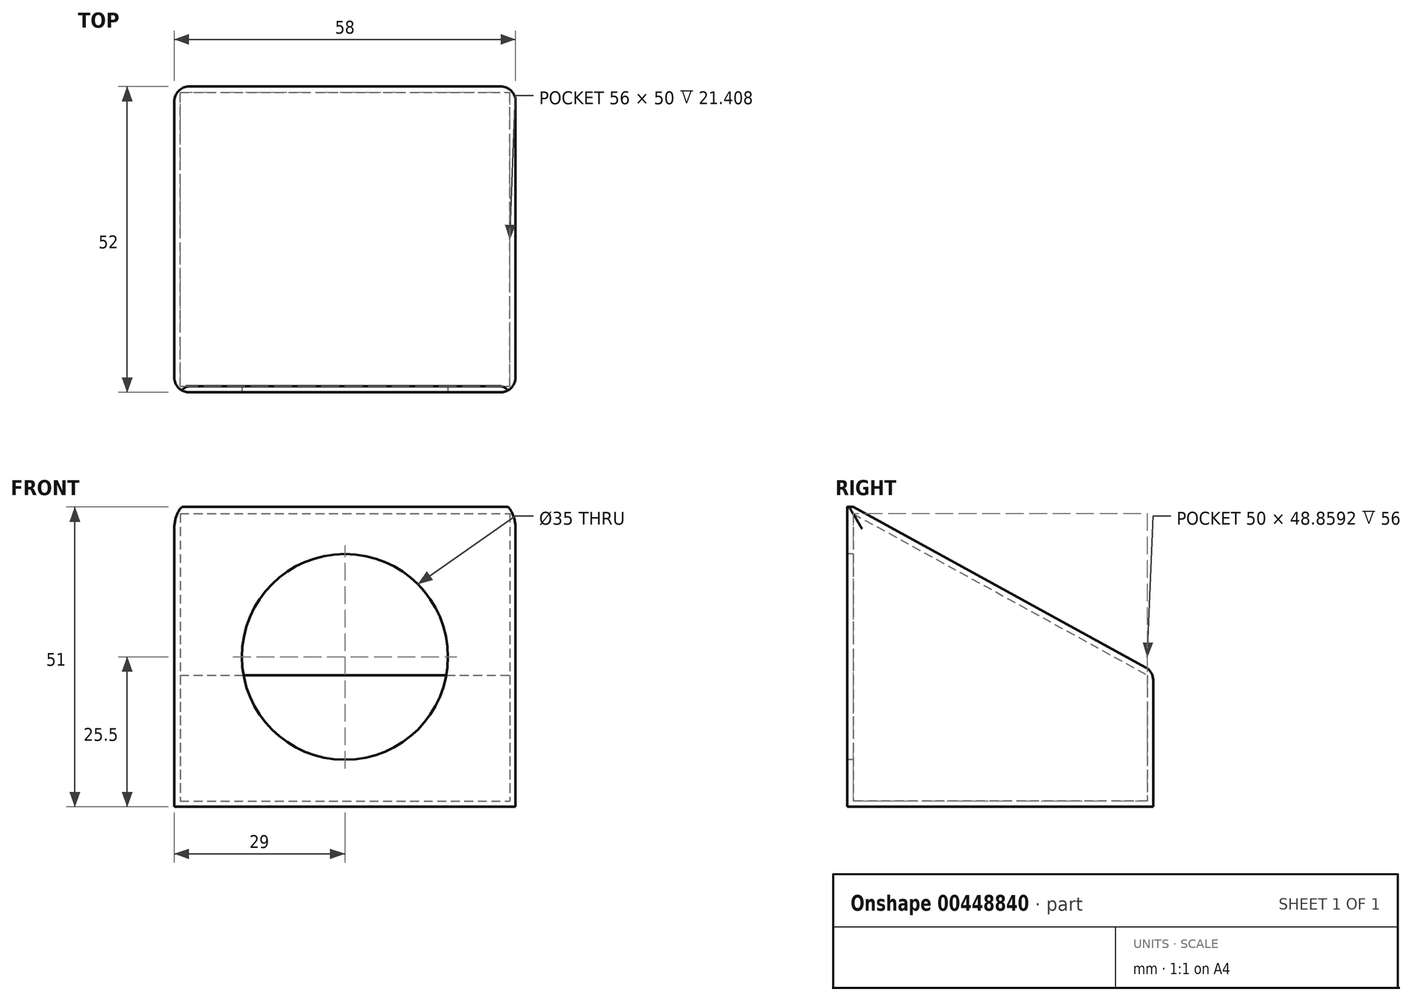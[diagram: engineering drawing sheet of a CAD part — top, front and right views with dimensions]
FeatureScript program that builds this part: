
annotation { "Feature Type Name" : "Feature", "Feature Type Description" : "" }
export const myFeature = defineFeature(function(context is Context, id is Id, definition is map)
    precondition{}
    {
        {
            var Q0;
            Q0=qCreatedBy(makeId("Top.planeOp"),FACE);
            var sketch = newSketch(context, id + "F0", { "sketchPlane" : qUnion([Q0])});
            skLineSegment(sketch, "E0.bottom", {"start": v(29, 26) * mm, "end": v(-29, 26) * mm});
            skLineSegment(sketch, "E0.top", {"start": v(29, -26) * mm, "end": v(-29, -26) * mm});
            skLineSegment(sketch, "E0.left", {"start": v(29, 26) * mm, "end": v(29, -26) * mm});
            skLineSegment(sketch, "E0.right", {"start": v(-29, 26) * mm, "end": v(-29, -26) * mm});
            skPoint(sketch, "E0.middle", {"position": v(0, 0) * mm});
            skSolve(sketch);
        }
        {
            var Q0;
            Q0=makeQuery(id+"F0.imprint","IMPRINT",FACE,{"disambiguationData":[TD([[makeQuery(id+"F0.imprint","IMPRINT",EDGE,{"derivedFrom":sQuery(id+"F0.wireOp",EDGE,"E0.bottom")}),1.0]])]});
            extrude(context, id + "F1", {"entities" : qUnion([Q0]), "depth" : 1 * mm});
        }
        {
            var Q0;
            Q0=makeQuery(id+"F1.opExtrude","CAP_FACE",FACE,{"disambiguationData":[OSD([sQuery(id+"F0.wireOp",EDGE,"E0.bottom"),sQuery(id+"F0.wireOp",EDGE,"E0.top"),sQuery(id+"F0.wireOp",EDGE,"E0.left"),sQuery(id+"F0.wireOp",EDGE,"E0.right")])],"isStart":false});
            var sketch = newSketch(context, id + "F2", { "sketchPlane" : qUnion([Q0])});
            skLineSegment(sketch, "E1", {"start": v(-29, 26) * mm, "end": v(-29, 25) * mm});
            skLineSegment(sketch, "E2", {"start": v(-29, 25) * mm, "end": v(29, 25) * mm});
            skLineSegment(sketch, "E3", {"start": v(-29, -26) * mm, "end": v(-29, -25) * mm});
            skLineSegment(sketch, "E4", {"start": v(-29, -25) * mm, "end": v(29, -25) * mm});
            skLineSegment(sketch, "E5", {"start": v(29, -25) * mm, "end": v(28, -25) * mm});
            skLineSegment(sketch, "E6", {"start": v(28, -25) * mm, "end": v(28, 25) * mm});
            skLineSegment(sketch, "E7", {"start": v(-29, -25) * mm, "end": v(-28, -25) * mm});
            skLineSegment(sketch, "E8", {"start": v(-28, -25) * mm, "end": v(-28, 25) * mm});
            skSolve(sketch);
        }
        {
            var Q0;
            Q0=makeQuery(id+"F2.imprint","IMPRINT",FACE,{"disambiguationData":[TD([[makeQuery(id+"F2.imprint","IMPRINT",EDGE,{"derivedFrom":sQuery(id+"F2.wireOp",EDGE,"E1")}),1.0]])]});
            extrude(context, id + "F3", {"entities" : qUnion([Q0]), "operationType" : NewBodyOperationType.ADD, "depth" : 22 * mm});
        }
        {
            var Q0;
            Q0=makeQuery(id+"F2.imprint","IMPRINT",FACE,{"disambiguationData":[TD([[makeQuery(id+"F2.imprint","IMPRINT",EDGE,{"derivedFrom":sQuery(id+"F2.wireOp",EDGE,"E3")}),1.0]])]});
            extrude(context, id + "F4", {"entities" : qUnion([Q0]), "operationType" : NewBodyOperationType.ADD, "depth" : 50 * mm});
        }
        {
            var Q0;
            Q0=makeQuery(id+"F4.boolean.opBoolean","MERGE",FACE,{"derivedFrom":[makeQuery(id+"F3.boolean.opBoolean","MERGE",FACE,{"derivedFrom":[makeQuery(id+"F1.opExtrude","SWEPT_FACE",FACE,{"disambiguationData":[OSD([sQuery(id+"F0.wireOp",EDGE,"E0.right")])]}),makeQuery(id+"F3.opExtrude","SWEPT_FACE",FACE,{"disambiguationData":[OSD([sQuery(id+"F2.wireOp",EDGE,"E1")])]})]}),makeQuery(id+"F4.opExtrude","SWEPT_FACE",FACE,{"disambiguationData":[OSD([sQuery(id+"F2.wireOp",EDGE,"E3")])]})]});
            var sketch = newSketch(context, id + "F5", { "sketchPlane" : qUnion([Q0])});
            skLineSegment(sketch, "E9", {"start": v(-26, 23) * mm, "end": v(25, 51) * mm});
            skSolve(sketch);
        }
        {
            var Q0;
            Q0=makeQuery(id+"F5.imprint","IMPRINT",FACE,{"disambiguationData":[TD([[makeQuery(id+"F5.imprint","IMPRINT",EDGE,{"derivedFrom":sQuery(id+"F5.wireOp",EDGE,"E9")}),-1.0]])]});
            extrude(context, id + "F6", {"entities" : qUnion([Q0]), "operationType" : NewBodyOperationType.ADD, "oppositeDirection" : true, "depth" : 1 * mm});
        }
        {
            var Q0;
            {var subQ0=sQuery(id+"F0.wireOp",EDGE,"E0.left");Q0=makeQuery(id+"F4.boolean.opBoolean","MERGE",FACE,{"derivedFrom":[makeQuery(id+"F3.boolean.opBoolean","MERGE",FACE,{"derivedFrom":[makeQuery(id+"F1.opExtrude","SWEPT_FACE",FACE,{"disambiguationData":[OSD([subQ0])]}),makeQuery(id+"F3.opExtrude","SWEPT_FACE",FACE,{"disambiguationData":[OSD([subQ0])]})]}),makeQuery(id+"F4.opExtrude","SWEPT_FACE",FACE,{"disambiguationData":[OSD([subQ0])]})]});}
            var sketch = newSketch(context, id + "F7", { "sketchPlane" : qUnion([Q0])});
            skLineSegment(sketch, "E10", {"start": v(-25, 51) * mm, "end": v(26, 23) * mm});
            skSolve(sketch);
        }
        {
            var Q0;
            Q0=makeQuery(id+"F7.imprint","IMPRINT",FACE,{"disambiguationData":[TD([[makeQuery(id+"F7.imprint","IMPRINT",EDGE,{"derivedFrom":sQuery(id+"F7.wireOp",EDGE,"E10")}),-1.0]])]});
            extrude(context, id + "F8", {"entities" : qUnion([Q0]), "operationType" : NewBodyOperationType.ADD, "oppositeDirection" : true, "depth" : 1 * mm});
        }
        {
            var Q0;
            Q0=makeQuery(id+"F8.opExtrude","SWEPT_FACE",FACE,{"disambiguationData":[OSD([sQuery(id+"F7.wireOp",EDGE,"E10")])]});
            var sketch = newSketch(context, id + "F9", { "sketchPlane" : qUnion([Q0])});
            skLineSegment(sketch, "E11", {"start": v(29, 11.72) * mm, "end": v(-29, 11.72) * mm});
            skLineSegment(sketch, "E12", {"start": v(-29, 11.72) * mm, "end": v(-29, -46.42) * mm});
            skLineSegment(sketch, "E13", {"start": v(-29, -46.42) * mm, "end": v(29, -46.46) * mm});
            skLineSegment(sketch, "E14", {"start": v(29, -46.46) * mm, "end": v(29, 11.72) * mm});
            skSolve(sketch);
        }
        {
            var Q0;
            {var subQ3=sQuery(id+"F9.wireOp",EDGE,"E12");Q0=makeQuery(id+"F9.imprint","IMPRINT",FACE,{"disambiguationData":[TD([[makeQuery(id+"F9.imprint","IMPRINT",EDGE,{"derivedFrom":subQ3}),1.0]])]});}
            extrude(context, id + "F10", {"entities" : qUnion([Q0]), "operationType" : NewBodyOperationType.ADD, "oppositeDirection" : true, "depth" : 1 * mm});
        }
        {
            var Q0;
            {var subQ0=sQuery(id+"F0.wireOp",EDGE,"E0.top");Q0=makeQuery(id+"F4.boolean.opBoolean","MERGE",FACE,{"derivedFrom":[makeQuery(id+"F1.opExtrude","SWEPT_FACE",FACE,{"disambiguationData":[OSD([subQ0])]}),makeQuery(id+"F4.opExtrude","SWEPT_FACE",FACE,{"disambiguationData":[OSD([subQ0])]})]});}
            var sketch = newSketch(context, id + "F11", { "sketchPlane" : qUnion([Q0])});
            skLineSegment(sketch, "E15", {"start": v(-29, 51) * mm, "end": v(29, 0) * mm});
            skLineSegment(sketch, "E16", {"start": v(29, 0) * mm, "end": v(29, 51) * mm});
            skLineSegment(sketch, "E17", {"start": v(29, 51) * mm, "end": v(-29, 0) * mm});
            skLineSegment(sketch, "E18", {"start": v(-29, 0) * mm, "end": v(0, 25.5) * mm});
            skSolve(sketch);
        }
        {
            var Q0;
            Q0=sQuery(id+"F11.wireOp",VERTEX,"E18.end");
            var Q1;
            Q1=makeQuery(id+"F1.opExtrude","SWEPT_BODY",BODY,{"disambiguationData":[OSD([sQuery(id+"F0.wireOp",EDGE,"E0.bottom"),sQuery(id+"F0.wireOp",EDGE,"E0.top"),sQuery(id+"F0.wireOp",EDGE,"E0.left"),sQuery(id+"F0.wireOp",EDGE,"E0.right")])]});
            hole(context, id + "F12", {"style" : HoleStyle.SIMPLE, "endStyle" : HoleEndStyle.BLIND, "holeDiameter" : 35 * mm, "holeDepth" : 2 * mm, "isTappedThrough" : true, "tappedDepth" : 12.7 * mm, "tapClearance" : 3, "locations" : qUnion([Q0]), "scope" : qUnion([Q1])});
        }
        {
            var Q0;
            {var subQ0=sQuery(id+"F0.wireOp",EDGE,"E0.top");Q0=makeQuery(id+"F4.boolean.opBoolean","MERGE",EDGE,{"derivedFrom":[makeQuery(id+"F1.opExtrude","SWEPT_EDGE",EDGE,{"disambiguationData":[OSD([subQ0,sQuery(id+"F0.wireOp",EDGE,"E0.right")])]}),makeQuery(id+"F4.opExtrude","SWEPT_EDGE",EDGE,{"disambiguationData":[OSD([subQ0,sQuery(id+"F2.wireOp",EDGE,"E3")])]})]});}
            var Q1;
            {var subQ0=sQuery(id+"F0.wireOp",EDGE,"E0.left");var subQ1=sQuery(id+"F0.wireOp",EDGE,"E0.top");Q1=makeQuery(id+"F4.boolean.opBoolean","MERGE",EDGE,{"derivedFrom":[makeQuery(id+"F1.opExtrude","SWEPT_EDGE",EDGE,{"disambiguationData":[OSD([subQ1,subQ0])]}),makeQuery(id+"F4.opExtrude","SWEPT_EDGE",EDGE,{"disambiguationData":[OSD([subQ1,subQ0])]})]});}
            var Q2;
            {var subQ0=sQuery(id+"F0.wireOp",EDGE,"E0.left");var subQ1=sQuery(id+"F0.wireOp",EDGE,"E0.bottom");Q2=makeQuery(id+"F3.boolean.opBoolean","MERGE",EDGE,{"derivedFrom":[makeQuery(id+"F1.opExtrude","SWEPT_EDGE",EDGE,{"disambiguationData":[OSD([subQ1,subQ0])]}),makeQuery(id+"F3.opExtrude","SWEPT_EDGE",EDGE,{"disambiguationData":[OSD([subQ1,subQ0])]})]});}
            var Q3;
            {var subQ0=sQuery(id+"F0.wireOp",EDGE,"E0.bottom");Q3=makeQuery(id+"F3.boolean.opBoolean","MERGE",EDGE,{"derivedFrom":[makeQuery(id+"F1.opExtrude","SWEPT_EDGE",EDGE,{"disambiguationData":[OSD([subQ0,sQuery(id+"F0.wireOp",EDGE,"E0.right")])]}),makeQuery(id+"F3.opExtrude","SWEPT_EDGE",EDGE,{"disambiguationData":[OSD([subQ0,sQuery(id+"F2.wireOp",EDGE,"E1")])]})]});}
            var Q4;
            {var subQ0=sQuery(id+"F0.wireOp",EDGE,"E0.bottom");var subQ4=sQuery(id+"F5.wireOp",EDGE,"E9");Q4=makeQuery(id+"F10.boolean.opBoolean","SPLIT",EDGE,{"disambiguationData":[TD([makeQuery(id+"F1.opExtrude","SWEPT_FACE",FACE,{"disambiguationData":[OSD([subQ0])]})])],"derivedFrom":makeQuery(id+"F6.opExtrude","CAP_EDGE",EDGE,{"disambiguationData":[OSD([subQ4])],"isStart":true})});}
            var Q5;
            {var subQ0=sQuery(id+"F0.wireOp",EDGE,"E0.bottom");var subQ1=makeQuery(id+"F3.opExtrude","CAP_EDGE",EDGE,{"disambiguationData":[OSD([subQ0])],"isStart":false});var subQ2=makeQuery(id+"F6.boolean.opBoolean","SPLIT",EDGE,{"derivedFrom":subQ1});Q5=makeQuery(id+"F10.boolean.opBoolean","MERGE",EDGE,{"derivedFrom":[makeQuery(id+"F6.boolean.opBoolean","MERGE",EDGE,{"derivedFrom":[subQ1,makeQuery(id+"F6.opExtrude","SWEPT_EDGE",EDGE,{"disambiguationData":[OSD([subQ0,sQuery(id+"F0.wireOp",EDGE,"E0.right"),sQuery(id+"F2.wireOp",EDGE,"E1"),sQuery(id+"F5.wireOp",EDGE,"E9")])]})]}),makeQuery(id+"F8.boolean.opBoolean","MERGE",EDGE,{"derivedFrom":[subQ2,makeQuery(id+"F8.opExtrude","SWEPT_EDGE",EDGE,{"disambiguationData":[OSD([subQ0,sQuery(id+"F0.wireOp",EDGE,"E0.left"),sQuery(id+"F7.wireOp",EDGE,"E10")])]})]}),makeQuery(id+"F8.boolean.opBoolean","SPLIT",EDGE,{"derivedFrom":subQ2}),makeQuery(id+"F10.opExtrude","CAP_EDGE",EDGE,{"disambiguationData":[OSD([sQuery(id+"F9.wireOp",EDGE,"E11")])],"isStart":true})]});}
            var Q6;
            Q6=makeQuery(id+"F8.opExtrude","CAP_EDGE",EDGE,{"disambiguationData":[OSD([sQuery(id+"F7.wireOp",EDGE,"E10")])],"isStart":true});
            fillet(context, id + "F13", {"entities" : qUnion([Q0, Q1, Q2, Q3, Q4, Q5, Q6]), "radius" : 2.54 * mm, "tangentPropagation" : true, "allowEdgeOverflow" : false});
        }
    });
